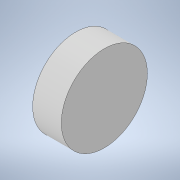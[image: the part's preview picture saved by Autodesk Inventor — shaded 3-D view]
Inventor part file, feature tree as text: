
AUTODESK INVENTOR PART (.ipt)
format: ipt  version: 2021.1 (Build 251245000, 245)  size: 98,304 bytes
history: native  units: in
note: dims shown in document units (in); Inventor stores cm internally (conversion verified against a paired STEP export)
features: extrude x1, sketch x1
ambient origin geometry x8: Origin, YZ Plane, XZ Plane, XY Plane, X Axis, Y Axis, Z Axis, Center Point
bodies: Solid1 (feature_tree)
feature tree (2):
  extrude  "Extrusion1"  Depth=1.4in TaperAngle=0.0deg
  sketch  "Sketch1"  dims[d0=4.2in d1=1.4in d2=0.0in]
